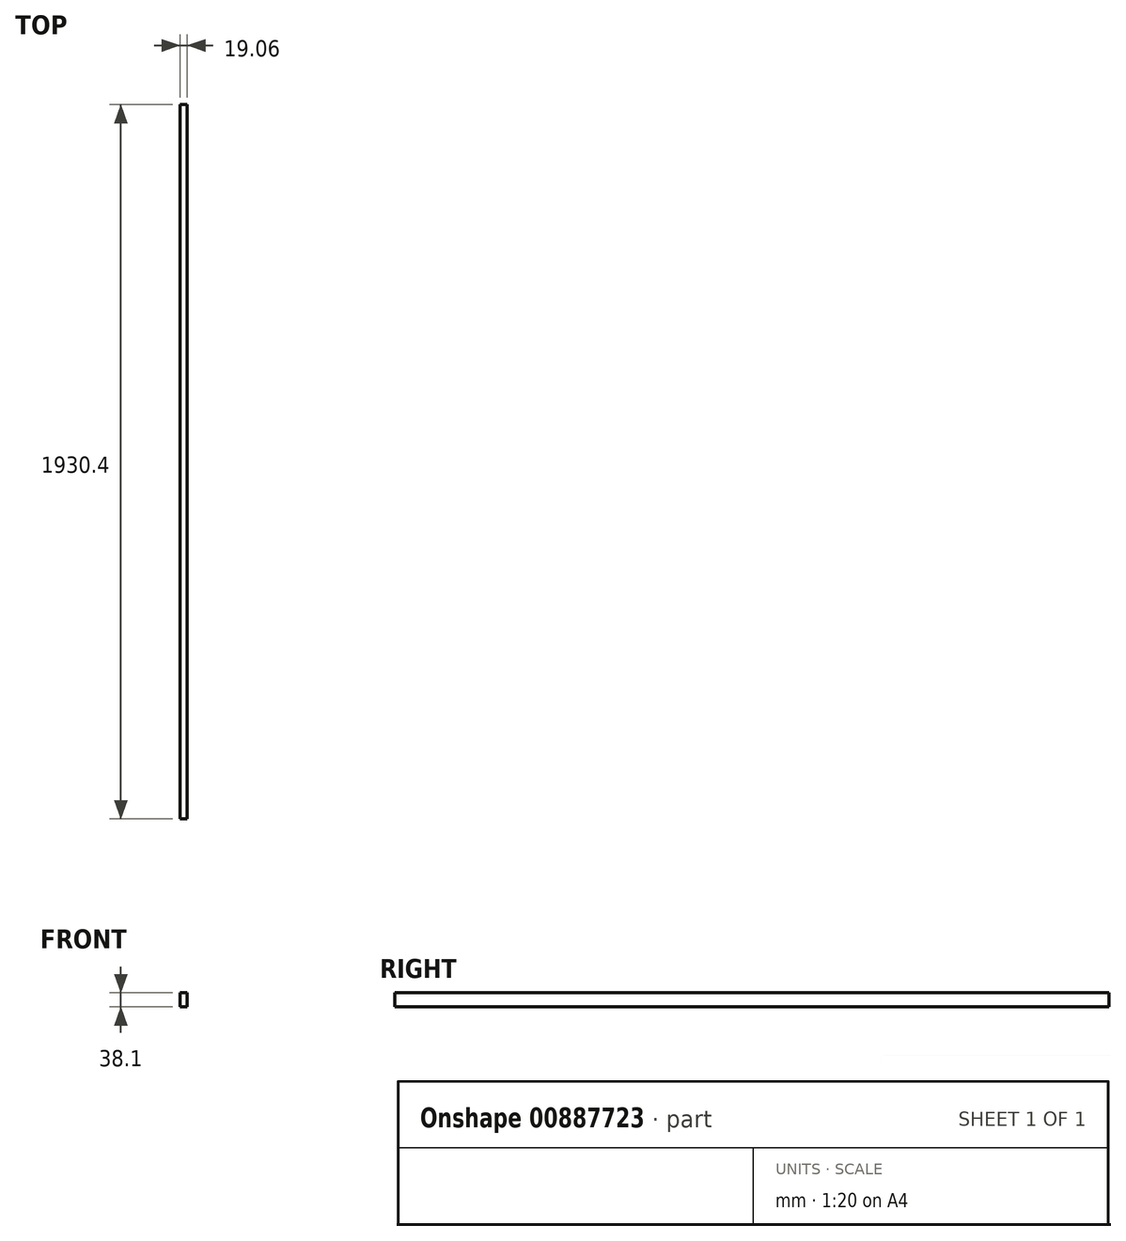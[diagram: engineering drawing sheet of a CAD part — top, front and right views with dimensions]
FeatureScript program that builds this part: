
annotation { "Feature Type Name" : "Feature", "Feature Type Description" : "" }
export const myFeature = defineFeature(function(context is Context, id is Id, definition is map)
    precondition{}
    {
        {
            var Q0;
            Q0=qCreatedBy(makeId("Front.planeOp"),FACE);
            var sketch = newSketch(context, id + "F0", { "sketchPlane" : qUnion([Q0])});
            skLineSegment(sketch, "E0.bottom", {"start": v(-9.52, 19.05) * mm, "end": v(9.53, 19.05) * mm});
            skLineSegment(sketch, "E0.top", {"start": v(-9.53, -19.05) * mm, "end": v(9.52, -19.05) * mm});
            skLineSegment(sketch, "E0.left", {"start": v(-9.52, 19.05) * mm, "end": v(-9.53, -19.05) * mm});
            skLineSegment(sketch, "E0.right", {"start": v(9.53, 19.05) * mm, "end": v(9.52, -19.05) * mm});
            skPoint(sketch, "E0.middle", {"position": v(0, 0) * mm});
            skSolve(sketch);
        }
        {
            var Q0;
            Q0=qSketchRegion(id+"F0",true);
            extrude(context, id + "F1", {"entities" : qUnion([Q0]), "endBound" : BoundingType.SYMMETRIC, "depth" : 1930.4 * mm, "offsetDistance" : 25.4 * mm});
        }
    });
